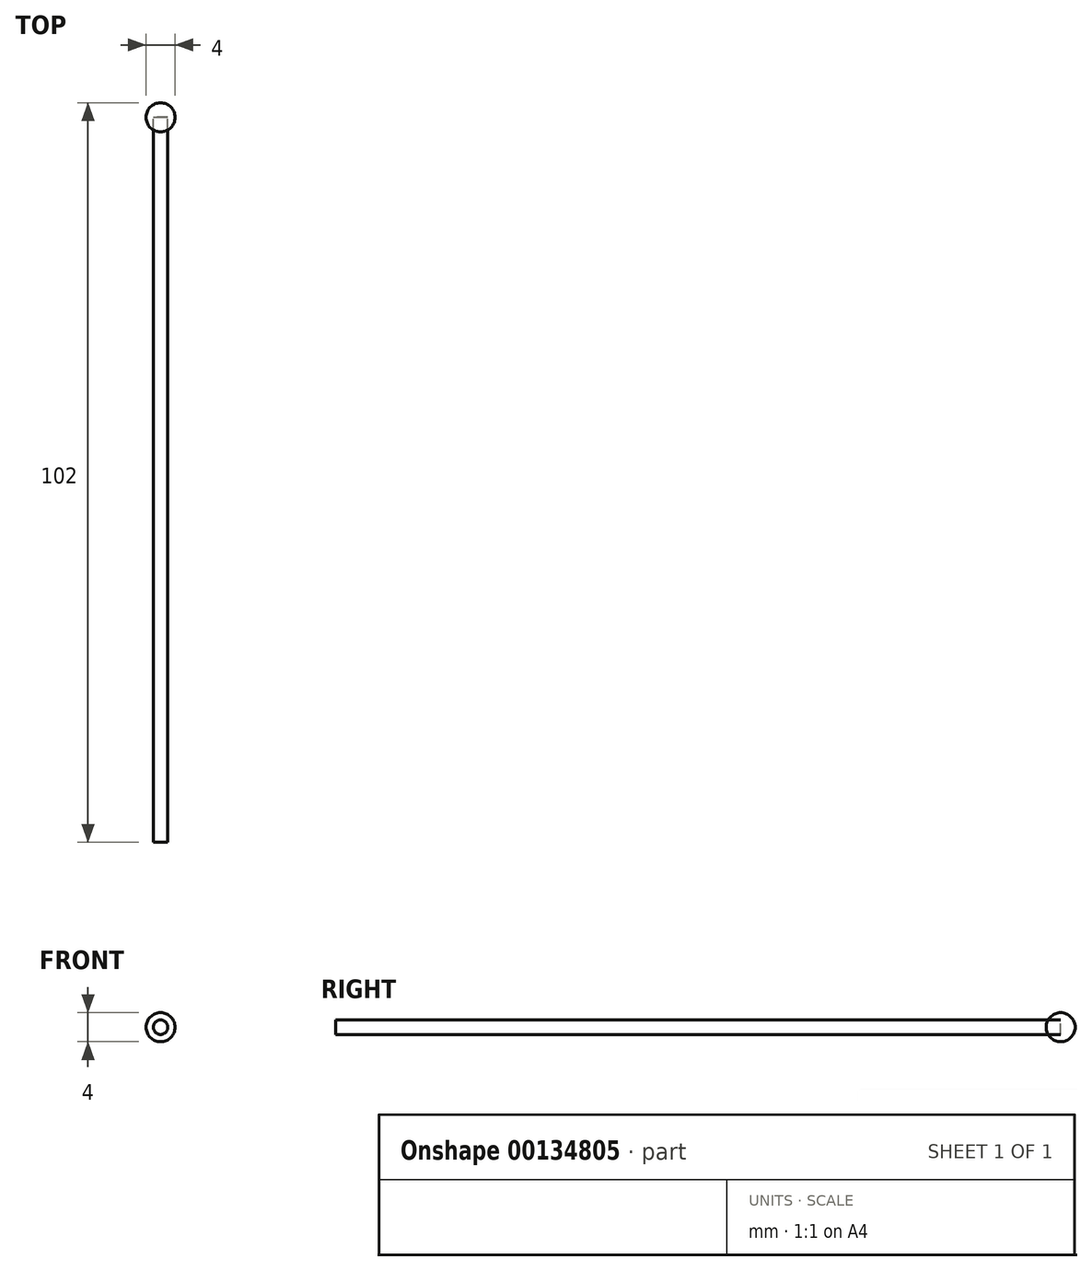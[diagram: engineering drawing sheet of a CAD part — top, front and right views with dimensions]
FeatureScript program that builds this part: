
annotation { "Feature Type Name" : "Feature", "Feature Type Description" : "" }
export const myFeature = defineFeature(function(context is Context, id is Id, definition is map)
    precondition{}
    {
        {
            var Q0;
            Q0=qCreatedBy(makeId("Front.planeOp"),FACE);
            var sketch = newSketch(context, id + "F0", { "sketchPlane" : qUnion([Q0])});
            skArc(sketch, "E0", {"start": v(0, 2) * mm, "mid": v(-2, 0) * mm, "end": v(0, -2) * mm});
            skLineSegment(sketch, "E1", {"start": v(0, 2) * mm, "end": v(0, -2) * mm});
            skSolve(sketch);
        }
        {
            var Q0;
            Q0=makeQuery(id+"F0.imprint","IMPRINT",FACE,{"disambiguationData":[TD([[makeQuery(id+"F0.imprint","IMPRINT",EDGE,{"derivedFrom":sQuery(id+"F0.wireOp",EDGE,"E0")}),1.0]])]});
            var Q1;
            Q1=sQuery(id+"F0.wireOp",EDGE,"E1");
            revolve(context, id + "F1", {"entities" : qUnion([Q0]), "axis" : qUnion([Q1]), "revolveType" : RevolveType.FULL});
        }
        {
            var Q0;
            Q0=qCreatedBy(makeId("Front.planeOp"),FACE);
            var sketch = newSketch(context, id + "F2", { "sketchPlane" : qUnion([Q0])});
            skCircle(sketch, "E2", {"center": v(0, 0) * mm, "radius": 1 * mm});
            skSolve(sketch);
        }
        {
            var Q0;
            Q0=makeQuery(id+"F2.imprint","IMPRINT",FACE,{"disambiguationData":[TD([[makeQuery(id+"F2.imprint","IMPRINT",EDGE,{"derivedFrom":sQuery(id+"F2.wireOp",EDGE,"E2")}),1.0]])]});
            extrude(context, id + "F3", {"entities" : qUnion([Q0]), "depth" : 100 * mm});
        }
    });
